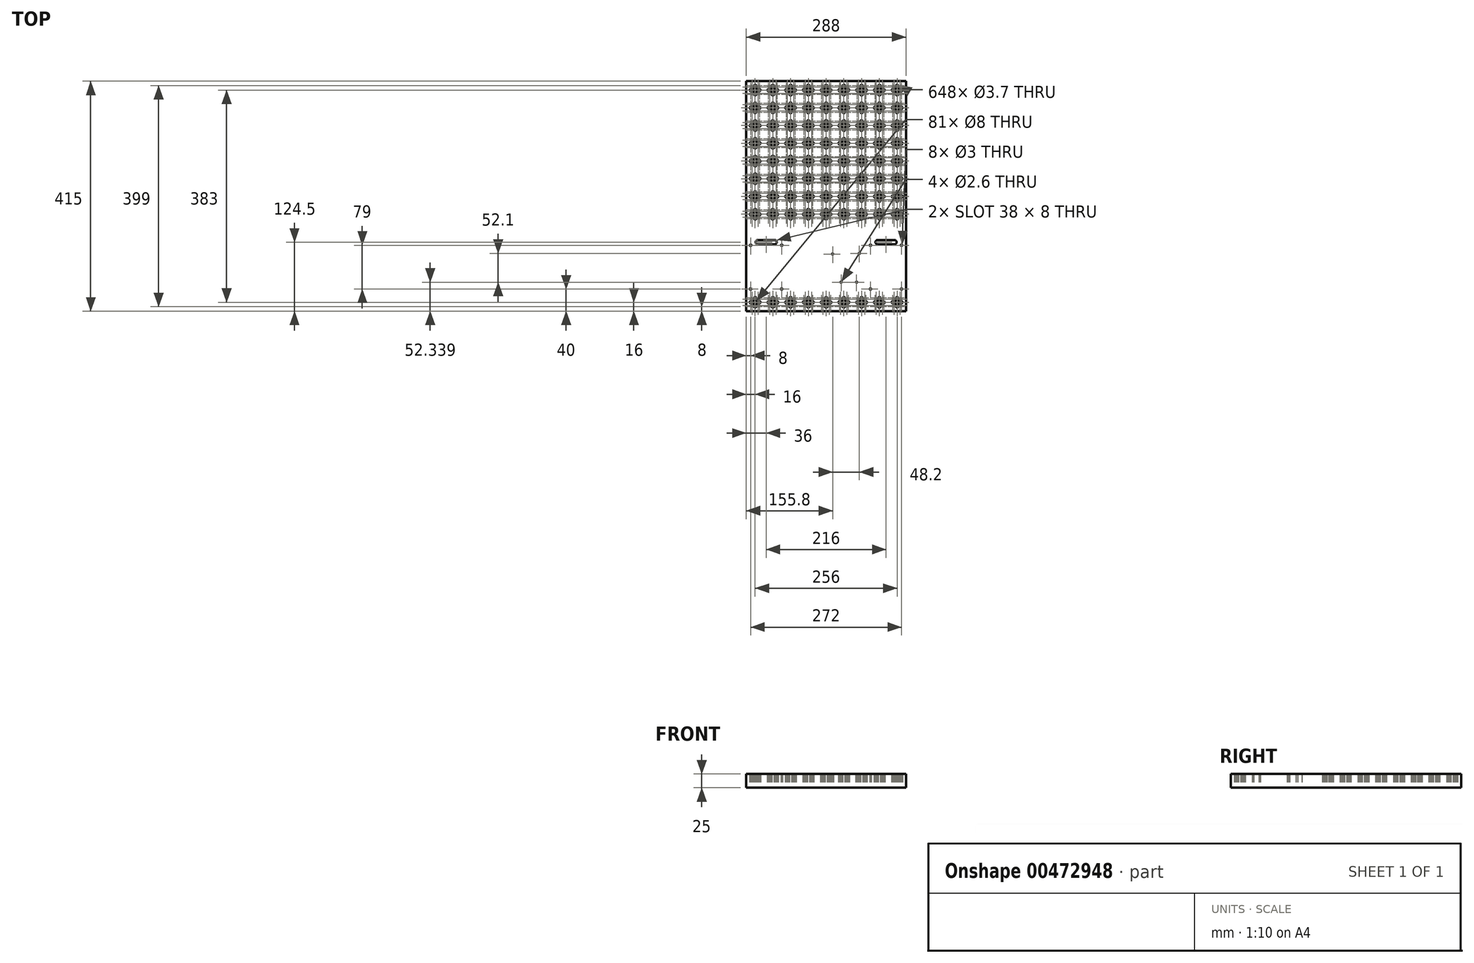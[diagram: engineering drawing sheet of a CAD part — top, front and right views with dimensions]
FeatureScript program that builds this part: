
annotation { "Feature Type Name" : "Feature", "Feature Type Description" : "" }
export const myFeature = defineFeature(function(context is Context, id is Id, definition is map)
    precondition{}
    {
        {
            var Q0;
            Q0=qCreatedBy(makeId("Top.planeOp"),FACE);
            var sketch = newSketch(context, id + "F0", { "sketchPlane" : qUnion([Q0])});
            skLineSegment(sketch, "E0.bottom", {"start": v(0, 0) * mm, "end": v(288, 0) * mm});
            skLineSegment(sketch, "E0.top", {"start": v(0, -415) * mm, "end": v(288, -415) * mm});
            skLineSegment(sketch, "E0.left", {"start": v(0, 0) * mm, "end": v(0, -415) * mm});
            skLineSegment(sketch, "E0.right", {"start": v(288, 0) * mm, "end": v(288, -415) * mm});
            skCircle(sketch, "E1", {"center": v(16, -407) * mm, "radius": 1.85 * mm});
            skCircle(sketch, "E2", {"center": v(16, -399) * mm, "radius": 4 * mm});
            skCircle(sketch, "E3.1.0", {"center": v(21.66, -404.66) * mm, "radius": 1.85 * mm});
            skCircle(sketch, "E3.2.0", {"center": v(24, -399) * mm, "radius": 1.85 * mm});
            skCircle(sketch, "E3.3.0", {"center": v(21.66, -393.34) * mm, "radius": 1.85 * mm});
            skCircle(sketch, "E3.4.0", {"center": v(16, -391) * mm, "radius": 1.85 * mm});
            skCircle(sketch, "E3.5.0", {"center": v(10.34, -393.34) * mm, "radius": 1.85 * mm});
            skCircle(sketch, "E3.6.0", {"center": v(8, -399) * mm, "radius": 1.85 * mm});
            skCircle(sketch, "E3.7.0", {"center": v(10.34, -404.66) * mm, "radius": 1.85 * mm});
            skCircle(sketch, "E4.1.0.0", {"center": v(42.34, -404.66) * mm, "radius": 1.85 * mm});
            skPoint(sketch, "E4.1.0.1", {"position": v(48, -399) * mm});
            skCircle(sketch, "E4.1.0.2", {"center": v(48, -391) * mm, "radius": 1.85 * mm});
            skCircle(sketch, "E4.1.0.3", {"center": v(53.66, -393.34) * mm, "radius": 1.85 * mm});
            skCircle(sketch, "E4.1.0.4", {"center": v(56, -399) * mm, "radius": 1.85 * mm});
            skCircle(sketch, "E4.1.0.5", {"center": v(53.66, -404.66) * mm, "radius": 1.85 * mm});
            skCircle(sketch, "E4.1.0.6", {"center": v(48, -399) * mm, "radius": 4 * mm});
            skCircle(sketch, "E4.1.0.7", {"center": v(48, -407) * mm, "radius": 1.85 * mm});
            skCircle(sketch, "E4.1.0.8", {"center": v(42.34, -393.34) * mm, "radius": 1.85 * mm});
            skCircle(sketch, "E4.1.0.9", {"center": v(40, -399) * mm, "radius": 1.85 * mm});
            skCircle(sketch, "E4.2.0.0", {"center": v(74.34, -404.66) * mm, "radius": 1.85 * mm});
            skPoint(sketch, "E4.2.0.1", {"position": v(80, -399) * mm});
            skCircle(sketch, "E4.2.0.2", {"center": v(80, -391) * mm, "radius": 1.85 * mm});
            skCircle(sketch, "E4.2.0.3", {"center": v(85.66, -393.34) * mm, "radius": 1.85 * mm});
            skCircle(sketch, "E4.2.0.4", {"center": v(88, -399) * mm, "radius": 1.85 * mm});
            skCircle(sketch, "E4.2.0.5", {"center": v(85.66, -404.66) * mm, "radius": 1.85 * mm});
            skCircle(sketch, "E4.2.0.6", {"center": v(80, -399) * mm, "radius": 4 * mm});
            skCircle(sketch, "E4.2.0.7", {"center": v(80, -407) * mm, "radius": 1.85 * mm});
            skCircle(sketch, "E4.2.0.8", {"center": v(74.34, -393.34) * mm, "radius": 1.85 * mm});
            skCircle(sketch, "E4.2.0.9", {"center": v(72, -399) * mm, "radius": 1.85 * mm});
            skCircle(sketch, "E4.3.0.0", {"center": v(106.34, -404.66) * mm, "radius": 1.85 * mm});
            skPoint(sketch, "E4.3.0.1", {"position": v(112, -399) * mm});
            skCircle(sketch, "E4.3.0.2", {"center": v(112, -391) * mm, "radius": 1.85 * mm});
            skCircle(sketch, "E4.3.0.3", {"center": v(117.66, -393.34) * mm, "radius": 1.85 * mm});
            skCircle(sketch, "E4.3.0.4", {"center": v(120, -399) * mm, "radius": 1.85 * mm});
            skCircle(sketch, "E4.3.0.5", {"center": v(117.66, -404.66) * mm, "radius": 1.85 * mm});
            skCircle(sketch, "E4.3.0.6", {"center": v(112, -399) * mm, "radius": 4 * mm});
            skCircle(sketch, "E4.3.0.7", {"center": v(112, -407) * mm, "radius": 1.85 * mm});
            skCircle(sketch, "E4.3.0.8", {"center": v(106.34, -393.34) * mm, "radius": 1.85 * mm});
            skCircle(sketch, "E4.3.0.9", {"center": v(104, -399) * mm, "radius": 1.85 * mm});
            skCircle(sketch, "E4.4.0.0", {"center": v(138.34, -404.66) * mm, "radius": 1.85 * mm});
            skPoint(sketch, "E4.4.0.1", {"position": v(144, -399) * mm});
            skCircle(sketch, "E4.4.0.2", {"center": v(144, -391) * mm, "radius": 1.85 * mm});
            skCircle(sketch, "E4.4.0.3", {"center": v(149.66, -393.34) * mm, "radius": 1.85 * mm});
            skCircle(sketch, "E4.4.0.4", {"center": v(152, -399) * mm, "radius": 1.85 * mm});
            skCircle(sketch, "E4.4.0.5", {"center": v(149.66, -404.66) * mm, "radius": 1.85 * mm});
            skCircle(sketch, "E4.4.0.6", {"center": v(144, -399) * mm, "radius": 4 * mm});
            skCircle(sketch, "E4.4.0.7", {"center": v(144, -407) * mm, "radius": 1.85 * mm});
            skCircle(sketch, "E4.4.0.8", {"center": v(138.34, -393.34) * mm, "radius": 1.85 * mm});
            skCircle(sketch, "E4.4.0.9", {"center": v(136, -399) * mm, "radius": 1.85 * mm});
            skCircle(sketch, "E4.5.0.0", {"center": v(170.34, -404.66) * mm, "radius": 1.85 * mm});
            skPoint(sketch, "E4.5.0.1", {"position": v(176, -399) * mm});
            skCircle(sketch, "E4.5.0.2", {"center": v(176, -391) * mm, "radius": 1.85 * mm});
            skCircle(sketch, "E4.5.0.3", {"center": v(181.66, -393.34) * mm, "radius": 1.85 * mm});
            skCircle(sketch, "E4.5.0.4", {"center": v(184, -399) * mm, "radius": 1.85 * mm});
            skCircle(sketch, "E4.5.0.5", {"center": v(181.66, -404.66) * mm, "radius": 1.85 * mm});
            skCircle(sketch, "E4.5.0.6", {"center": v(176, -399) * mm, "radius": 4 * mm});
            skCircle(sketch, "E4.5.0.7", {"center": v(176, -407) * mm, "radius": 1.85 * mm});
            skCircle(sketch, "E4.5.0.8", {"center": v(170.34, -393.34) * mm, "radius": 1.85 * mm});
            skCircle(sketch, "E4.5.0.9", {"center": v(168, -399) * mm, "radius": 1.85 * mm});
            skCircle(sketch, "E4.6.0.0", {"center": v(202.34, -404.66) * mm, "radius": 1.85 * mm});
            skPoint(sketch, "E4.6.0.1", {"position": v(208, -399) * mm});
            skCircle(sketch, "E4.6.0.2", {"center": v(208, -391) * mm, "radius": 1.85 * mm});
            skCircle(sketch, "E4.6.0.3", {"center": v(213.66, -393.34) * mm, "radius": 1.85 * mm});
            skCircle(sketch, "E4.6.0.4", {"center": v(216, -399) * mm, "radius": 1.85 * mm});
            skCircle(sketch, "E4.6.0.5", {"center": v(213.66, -404.66) * mm, "radius": 1.85 * mm});
            skCircle(sketch, "E4.6.0.6", {"center": v(208, -399) * mm, "radius": 4 * mm});
            skCircle(sketch, "E4.6.0.7", {"center": v(208, -407) * mm, "radius": 1.85 * mm});
            skCircle(sketch, "E4.6.0.8", {"center": v(202.34, -393.34) * mm, "radius": 1.85 * mm});
            skCircle(sketch, "E4.6.0.9", {"center": v(200, -399) * mm, "radius": 1.85 * mm});
            skCircle(sketch, "E4.7.0.0", {"center": v(234.34, -404.66) * mm, "radius": 1.85 * mm});
            skPoint(sketch, "E4.7.0.1", {"position": v(240, -399) * mm});
            skCircle(sketch, "E4.7.0.2", {"center": v(240, -391) * mm, "radius": 1.85 * mm});
            skCircle(sketch, "E4.7.0.3", {"center": v(245.66, -393.34) * mm, "radius": 1.85 * mm});
            skCircle(sketch, "E4.7.0.4", {"center": v(248, -399) * mm, "radius": 1.85 * mm});
            skCircle(sketch, "E4.7.0.5", {"center": v(245.66, -404.66) * mm, "radius": 1.85 * mm});
            skCircle(sketch, "E4.7.0.6", {"center": v(240, -399) * mm, "radius": 4 * mm});
            skCircle(sketch, "E4.7.0.7", {"center": v(240, -407) * mm, "radius": 1.85 * mm});
            skCircle(sketch, "E4.7.0.8", {"center": v(234.34, -393.34) * mm, "radius": 1.85 * mm});
            skCircle(sketch, "E4.7.0.9", {"center": v(232, -399) * mm, "radius": 1.85 * mm});
            skCircle(sketch, "E4.8.0.0", {"center": v(266.34, -404.66) * mm, "radius": 1.85 * mm});
            skPoint(sketch, "E4.8.0.1", {"position": v(272, -399) * mm});
            skCircle(sketch, "E4.8.0.2", {"center": v(272, -391) * mm, "radius": 1.85 * mm});
            skCircle(sketch, "E4.8.0.3", {"center": v(277.66, -393.34) * mm, "radius": 1.85 * mm});
            skCircle(sketch, "E4.8.0.4", {"center": v(280, -399) * mm, "radius": 1.85 * mm});
            skCircle(sketch, "E4.8.0.5", {"center": v(277.66, -404.66) * mm, "radius": 1.85 * mm});
            skCircle(sketch, "E4.8.0.6", {"center": v(272, -399) * mm, "radius": 4 * mm});
            skCircle(sketch, "E4.8.0.7", {"center": v(272, -407) * mm, "radius": 1.85 * mm});
            skCircle(sketch, "E4.8.0.8", {"center": v(266.34, -393.34) * mm, "radius": 1.85 * mm});
            skCircle(sketch, "E4.8.0.9", {"center": v(264, -399) * mm, "radius": 1.85 * mm});
            skLineSegment(sketch, "E4.direction1", {"start": v(10.34, -404.66) * mm, "end": v(42.34, -404.66) * mm, "construction": true});
            skLineSegment(sketch, "E5", {"start": v(0, -207.5) * mm, "end": v(288, -207.5) * mm, "construction": true});
            skCircle(sketch, "E6.MirrorC", {"center": v(8, -16) * mm, "radius": 1.85 * mm});
            skCircle(sketch, "E7.MirrorC", {"center": v(48, -8) * mm, "radius": 1.85 * mm});
            skCircle(sketch, "E8.MirrorC", {"center": v(240, -16) * mm, "radius": 4 * mm});
            skCircle(sketch, "E9.MirrorC", {"center": v(53.66, -10.34) * mm, "radius": 1.85 * mm});
            skCircle(sketch, "E10.MirrorC", {"center": v(208, -16) * mm, "radius": 4 * mm});
            skCircle(sketch, "E11.MirrorC", {"center": v(144, -16) * mm, "radius": 4 * mm});
            skCircle(sketch, "E12.MirrorC", {"center": v(56, -16) * mm, "radius": 1.85 * mm});
            skCircle(sketch, "E13.MirrorC", {"center": v(112, -16) * mm, "radius": 4 * mm});
            skCircle(sketch, "E14.MirrorC", {"center": v(16, -16) * mm, "radius": 4 * mm});
            skCircle(sketch, "E15.MirrorC", {"center": v(10.34, -10.34) * mm, "radius": 1.85 * mm});
            skCircle(sketch, "E16.MirrorC", {"center": v(176, -16) * mm, "radius": 4 * mm});
            skCircle(sketch, "E17.MirrorC", {"center": v(42.34, -10.34) * mm, "radius": 1.85 * mm});
            skCircle(sketch, "E18.MirrorC", {"center": v(42.34, -21.66) * mm, "radius": 1.85 * mm});
            skCircle(sketch, "E19.MirrorC", {"center": v(277.66, -10.34) * mm, "radius": 1.85 * mm});
            skCircle(sketch, "E20.MirrorC", {"center": v(40, -16) * mm, "radius": 1.85 * mm});
            skCircle(sketch, "E21.MirrorC", {"center": v(80, -16) * mm, "radius": 4 * mm});
            skCircle(sketch, "E22.MirrorC", {"center": v(272, -16) * mm, "radius": 4 * mm});
            skCircle(sketch, "E23.MirrorC", {"center": v(48, -16) * mm, "radius": 4 * mm});
            skCircle(sketch, "E24.MirrorC", {"center": v(272, -8) * mm, "radius": 1.85 * mm});
            skCircle(sketch, "E25.MirrorC", {"center": v(21.66, -21.66) * mm, "radius": 1.85 * mm});
            skCircle(sketch, "E26.MirrorC", {"center": v(10.34, -21.66) * mm, "radius": 1.85 * mm});
            skCircle(sketch, "E27.MirrorC", {"center": v(117.66, -21.66) * mm, "radius": 1.85 * mm});
            skCircle(sketch, "E28.MirrorC", {"center": v(74.34, -10.34) * mm, "radius": 1.85 * mm});
            skCircle(sketch, "E29.MirrorC", {"center": v(234.34, -21.66) * mm, "radius": 1.85 * mm});
            skCircle(sketch, "E30.MirrorC", {"center": v(248, -16) * mm, "radius": 1.85 * mm});
            skCircle(sketch, "E31.MirrorC", {"center": v(117.66, -10.34) * mm, "radius": 1.85 * mm});
            skCircle(sketch, "E32.MirrorC", {"center": v(280, -16) * mm, "radius": 1.85 * mm});
            skCircle(sketch, "E33.MirrorC", {"center": v(176, -8) * mm, "radius": 1.85 * mm});
            skCircle(sketch, "E34.MirrorC", {"center": v(176, -24) * mm, "radius": 1.85 * mm});
            skCircle(sketch, "E35.MirrorC", {"center": v(104, -16) * mm, "radius": 1.85 * mm});
            skLineSegment(sketch, "E36.MirrorCS", {"start": v(10.34, -10.34) * mm, "end": v(42.34, -10.34) * mm, "construction": true});
            skCircle(sketch, "E37.MirrorC", {"center": v(112, -8) * mm, "radius": 1.85 * mm});
            skCircle(sketch, "E38.MirrorC", {"center": v(181.66, -10.34) * mm, "radius": 1.85 * mm});
            skCircle(sketch, "E39.MirrorC", {"center": v(72, -16) * mm, "radius": 1.85 * mm});
            skCircle(sketch, "E40.MirrorC", {"center": v(85.66, -21.66) * mm, "radius": 1.85 * mm});
            skCircle(sketch, "E41.MirrorC", {"center": v(245.66, -10.34) * mm, "radius": 1.85 * mm});
            skCircle(sketch, "E42.MirrorC", {"center": v(264, -16) * mm, "radius": 1.85 * mm});
            skCircle(sketch, "E43.MirrorC", {"center": v(272, -24) * mm, "radius": 1.85 * mm});
            skCircle(sketch, "E44.MirrorC", {"center": v(74.34, -21.66) * mm, "radius": 1.85 * mm});
            skCircle(sketch, "E45.MirrorC", {"center": v(149.66, -10.34) * mm, "radius": 1.85 * mm});
            skCircle(sketch, "E46.MirrorC", {"center": v(120, -16) * mm, "radius": 1.85 * mm});
            skCircle(sketch, "E47.MirrorC", {"center": v(80, -8) * mm, "radius": 1.85 * mm});
            skCircle(sketch, "E48.MirrorC", {"center": v(24, -16) * mm, "radius": 1.85 * mm});
            skCircle(sketch, "E49.MirrorC", {"center": v(16, -24) * mm, "radius": 1.85 * mm});
            skCircle(sketch, "E50.MirrorC", {"center": v(112, -24) * mm, "radius": 1.85 * mm});
            skCircle(sketch, "E51.MirrorC", {"center": v(138.34, -21.66) * mm, "radius": 1.85 * mm});
            skCircle(sketch, "E52.MirrorC", {"center": v(106.34, -10.34) * mm, "radius": 1.85 * mm});
            skCircle(sketch, "E53.MirrorC", {"center": v(106.34, -21.66) * mm, "radius": 1.85 * mm});
            skCircle(sketch, "E54.MirrorC", {"center": v(232, -16) * mm, "radius": 1.85 * mm});
            skCircle(sketch, "E55.MirrorC", {"center": v(152, -16) * mm, "radius": 1.85 * mm});
            skCircle(sketch, "E56.MirrorC", {"center": v(168, -16) * mm, "radius": 1.85 * mm});
            skCircle(sketch, "E57.MirrorC", {"center": v(48, -24) * mm, "radius": 1.85 * mm});
            skCircle(sketch, "E58.MirrorC", {"center": v(202.34, -21.66) * mm, "radius": 1.85 * mm});
            skCircle(sketch, "E59.MirrorC", {"center": v(53.66, -21.66) * mm, "radius": 1.85 * mm});
            skCircle(sketch, "E60.MirrorC", {"center": v(202.34, -10.34) * mm, "radius": 1.85 * mm});
            skCircle(sketch, "E61.MirrorC", {"center": v(85.66, -10.34) * mm, "radius": 1.85 * mm});
            skCircle(sketch, "E62.MirrorC", {"center": v(149.66, -21.66) * mm, "radius": 1.85 * mm});
            skCircle(sketch, "E63.MirrorC", {"center": v(170.34, -10.34) * mm, "radius": 1.85 * mm});
            skCircle(sketch, "E64.MirrorC", {"center": v(234.34, -10.34) * mm, "radius": 1.85 * mm});
            skCircle(sketch, "E65.MirrorC", {"center": v(266.34, -21.66) * mm, "radius": 1.85 * mm});
            skCircle(sketch, "E66.MirrorC", {"center": v(181.66, -21.66) * mm, "radius": 1.85 * mm});
            skCircle(sketch, "E67.MirrorC", {"center": v(88, -16) * mm, "radius": 1.85 * mm});
            skCircle(sketch, "E68.MirrorC", {"center": v(213.66, -21.66) * mm, "radius": 1.85 * mm});
            skCircle(sketch, "E69.MirrorC", {"center": v(266.34, -10.34) * mm, "radius": 1.85 * mm});
            skCircle(sketch, "E70.MirrorC", {"center": v(208, -8) * mm, "radius": 1.85 * mm});
            skCircle(sketch, "E71.MirrorC", {"center": v(136, -16) * mm, "radius": 1.85 * mm});
            skCircle(sketch, "E72.MirrorC", {"center": v(208, -24) * mm, "radius": 1.85 * mm});
            skCircle(sketch, "E73.MirrorC", {"center": v(277.66, -21.66) * mm, "radius": 1.85 * mm});
            skCircle(sketch, "E74.MirrorC", {"center": v(240, -24) * mm, "radius": 1.85 * mm});
            skCircle(sketch, "E75.MirrorC", {"center": v(144, -8) * mm, "radius": 1.85 * mm});
            skCircle(sketch, "E76.MirrorC", {"center": v(138.34, -10.34) * mm, "radius": 1.85 * mm});
            skCircle(sketch, "E77.MirrorC", {"center": v(80, -24) * mm, "radius": 1.85 * mm});
            skCircle(sketch, "E78.MirrorC", {"center": v(21.66, -10.34) * mm, "radius": 1.85 * mm});
            skCircle(sketch, "E79.MirrorC", {"center": v(16, -8) * mm, "radius": 1.85 * mm});
            skCircle(sketch, "E80.MirrorC", {"center": v(170.34, -21.66) * mm, "radius": 1.85 * mm});
            skCircle(sketch, "E81.MirrorC", {"center": v(200, -16) * mm, "radius": 1.85 * mm});
            skCircle(sketch, "E82.MirrorC", {"center": v(245.66, -21.66) * mm, "radius": 1.85 * mm});
            skCircle(sketch, "E83.MirrorC", {"center": v(213.66, -10.34) * mm, "radius": 1.85 * mm});
            skCircle(sketch, "E84.MirrorC", {"center": v(240, -8) * mm, "radius": 1.85 * mm});
            skCircle(sketch, "E85.MirrorC", {"center": v(144, -24) * mm, "radius": 1.85 * mm});
            skCircle(sketch, "E86.MirrorC", {"center": v(216, -16) * mm, "radius": 1.85 * mm});
            skCircle(sketch, "E87.MirrorC", {"center": v(184, -16) * mm, "radius": 1.85 * mm});
            skCircle(sketch, "E88", {"center": v(280, -375) * mm, "radius": 1.5 * mm});
            skCircle(sketch, "E89", {"center": v(280, -296) * mm, "radius": 1.5 * mm});
            skCircle(sketch, "E90", {"center": v(224, -296) * mm, "radius": 1.5 * mm});
            skCircle(sketch, "E91", {"center": v(224, -375) * mm, "radius": 1.5 * mm});
            skPoint(sketch, "E92.startSnap0", {"position": v(144, 0) * mm});
            skLineSegment(sketch, "E93", {"start": v(144, 0) * mm, "end": v(144, -415) * mm, "construction": true});
            skCircle(sketch, "E94.MirrorC", {"center": v(8, -375) * mm, "radius": 1.5 * mm});
            skCircle(sketch, "E95.MirrorC", {"center": v(64, -296) * mm, "radius": 1.5 * mm});
            skCircle(sketch, "E96.MirrorC", {"center": v(64, -375) * mm, "radius": 1.5 * mm});
            skCircle(sketch, "E97.MirrorC", {"center": v(8, -296) * mm, "radius": 1.5 * mm});
            skLineSegment(sketch, "E98.bottom", {"start": v(267, -286.5) * mm, "end": v(237, -286.5) * mm});
            skLineSegment(sketch, "E98.top", {"start": v(267, -294.5) * mm, "end": v(237, -294.5) * mm});
            skLineSegment(sketch, "E98.left", {"start": v(271, -290.5) * mm, "end": v(271, -290.5) * mm});
            skLineSegment(sketch, "E98.right", {"start": v(233, -290.5) * mm, "end": v(233, -290.5) * mm});
            skLineSegment(sketch, "E99.MirrorCS", {"start": v(17, -290.5) * mm, "end": v(17, -290.5) * mm});
            skLineSegment(sketch, "E100.MirrorCS", {"start": v(55, -290.5) * mm, "end": v(55, -290.5) * mm});
            skLineSegment(sketch, "E101.MirrorCS", {"start": v(21, -286.5) * mm, "end": v(51, -286.5) * mm});
            skLineSegment(sketch, "E102.MirrorCS", {"start": v(21, -294.5) * mm, "end": v(51, -294.5) * mm});
            skPoint(sketch, "E103.visualSharp", {"position": v(233, -286.5) * mm});
            skArc(sketch, "E103.filletArc", {"start": v(237, -286.5) * mm, "mid": v(234.17, -287.67) * mm, "end": v(233, -290.5) * mm});
            skPoint(sketch, "E104.visualSharp", {"position": v(271, -294.5) * mm});
            skArc(sketch, "E104.filletArc", {"start": v(267, -294.5) * mm, "mid": v(269.83, -293.33) * mm, "end": v(271, -290.5) * mm});
            skPoint(sketch, "E105.visualSharp", {"position": v(233, -294.5) * mm});
            skArc(sketch, "E105.filletArc", {"start": v(233, -290.5) * mm, "mid": v(234.17, -293.33) * mm, "end": v(237, -294.5) * mm});
            skPoint(sketch, "E106.visualSharp", {"position": v(55, -286.5) * mm});
            skArc(sketch, "E106.filletArc", {"start": v(55, -290.5) * mm, "mid": v(53.83, -287.67) * mm, "end": v(51, -286.5) * mm});
            skPoint(sketch, "E107.visualSharp", {"position": v(17, -294.5) * mm});
            skArc(sketch, "E107.filletArc", {"start": v(17, -290.5) * mm, "mid": v(18.17, -293.33) * mm, "end": v(21, -294.5) * mm});
            skPoint(sketch, "E108.visualSharp", {"position": v(55, -294.5) * mm});
            skArc(sketch, "E108.filletArc", {"start": v(51, -294.5) * mm, "mid": v(53.83, -293.33) * mm, "end": v(55, -290.5) * mm});
            skPoint(sketch, "E109.visualSharp", {"position": v(17, -286.5) * mm});
            skArc(sketch, "E109.filletArc", {"start": v(21, -286.5) * mm, "mid": v(18.17, -287.67) * mm, "end": v(17, -290.5) * mm});
            skPoint(sketch, "E110.visualSharp", {"position": v(271, -286.5) * mm});
            skArc(sketch, "E110.filletArc", {"start": v(271, -290.5) * mm, "mid": v(269.83, -287.67) * mm, "end": v(267, -286.5) * mm});
            skSolve(sketch);
        }
        {
            var Q0;
            Q0=makeQuery(id+"F0.imprint","IMPRINT",FACE,{"disambiguationData":[TD([[makeQuery(id+"F0.imprint","IMPRINT",EDGE,{"derivedFrom":sQuery(id+"F0.wireOp",EDGE,"E0.bottom")}),-1.0]])]});
            var sketch = newSketch(context, id + "F1", { "sketchPlane" : qUnion([Q0])});
            skCircle(sketch, "E111", {"center": v(24, -48) * mm, "radius": 1.85 * mm});
            skCircle(sketch, "E112", {"center": v(16, -48) * mm, "radius": 4 * mm});
            skCircle(sketch, "E113.1.0", {"center": v(21.66, -42.34) * mm, "radius": 1.85 * mm});
            skCircle(sketch, "E113.2.0", {"center": v(16, -40) * mm, "radius": 1.85 * mm});
            skCircle(sketch, "E114.1.3.0", {"center": v(10.34, -42.34) * mm, "radius": 1.85 * mm});
            skCircle(sketch, "E114.1.4.0", {"center": v(8, -48) * mm, "radius": 1.85 * mm});
            skCircle(sketch, "E114.1.5.0", {"center": v(10.34, -53.66) * mm, "radius": 1.85 * mm});
            skCircle(sketch, "E114.1.6.0", {"center": v(16, -56) * mm, "radius": 1.85 * mm});
            skCircle(sketch, "E114.1.7.0", {"center": v(21.66, -53.66) * mm, "radius": 1.85 * mm});
            skCircle(sketch, "E115.0.1.0", {"center": v(16, -80) * mm, "radius": 4 * mm});
            skCircle(sketch, "E115.0.1.1", {"center": v(16, -72) * mm, "radius": 1.85 * mm});
            skCircle(sketch, "E115.0.1.2", {"center": v(21.66, -74.34) * mm, "radius": 1.85 * mm});
            skCircle(sketch, "E115.0.1.3", {"center": v(24, -80) * mm, "radius": 1.85 * mm});
            skCircle(sketch, "E115.0.1.4", {"center": v(21.66, -85.66) * mm, "radius": 1.85 * mm});
            skCircle(sketch, "E115.0.1.5", {"center": v(16, -88) * mm, "radius": 1.85 * mm});
            skCircle(sketch, "E115.0.1.6", {"center": v(10.34, -85.66) * mm, "radius": 1.85 * mm});
            skCircle(sketch, "E115.0.1.7", {"center": v(8, -80) * mm, "radius": 1.85 * mm});
            skCircle(sketch, "E115.0.1.8", {"center": v(10.34, -74.34) * mm, "radius": 1.85 * mm});
            skCircle(sketch, "E115.0.2.0", {"center": v(16, -112) * mm, "radius": 4 * mm});
            skCircle(sketch, "E115.0.2.1", {"center": v(16, -104) * mm, "radius": 1.85 * mm});
            skCircle(sketch, "E115.0.2.2", {"center": v(21.66, -106.34) * mm, "radius": 1.85 * mm});
            skCircle(sketch, "E115.0.2.3", {"center": v(24, -112) * mm, "radius": 1.85 * mm});
            skCircle(sketch, "E115.0.2.4", {"center": v(21.66, -117.66) * mm, "radius": 1.85 * mm});
            skCircle(sketch, "E115.0.2.5", {"center": v(16, -120) * mm, "radius": 1.85 * mm});
            skCircle(sketch, "E115.0.2.6", {"center": v(10.34, -117.66) * mm, "radius": 1.85 * mm});
            skCircle(sketch, "E115.0.2.7", {"center": v(8, -112) * mm, "radius": 1.85 * mm});
            skCircle(sketch, "E115.0.2.8", {"center": v(10.34, -106.34) * mm, "radius": 1.85 * mm});
            skCircle(sketch, "E115.0.3.0", {"center": v(16, -144) * mm, "radius": 4 * mm});
            skCircle(sketch, "E115.0.3.1", {"center": v(16, -136) * mm, "radius": 1.85 * mm});
            skCircle(sketch, "E115.0.3.2", {"center": v(21.66, -138.34) * mm, "radius": 1.85 * mm});
            skCircle(sketch, "E115.0.3.3", {"center": v(24, -144) * mm, "radius": 1.85 * mm});
            skCircle(sketch, "E115.0.3.4", {"center": v(21.66, -149.66) * mm, "radius": 1.85 * mm});
            skCircle(sketch, "E115.0.3.5", {"center": v(16, -152) * mm, "radius": 1.85 * mm});
            skCircle(sketch, "E115.0.3.6", {"center": v(10.34, -149.66) * mm, "radius": 1.85 * mm});
            skCircle(sketch, "E115.0.3.7", {"center": v(8, -144) * mm, "radius": 1.85 * mm});
            skCircle(sketch, "E115.0.3.8", {"center": v(10.34, -138.34) * mm, "radius": 1.85 * mm});
            skCircle(sketch, "E115.0.4.0", {"center": v(16, -176) * mm, "radius": 4 * mm});
            skCircle(sketch, "E115.0.4.1", {"center": v(16, -168) * mm, "radius": 1.85 * mm});
            skCircle(sketch, "E115.0.4.2", {"center": v(21.66, -170.34) * mm, "radius": 1.85 * mm});
            skCircle(sketch, "E115.0.4.3", {"center": v(24, -176) * mm, "radius": 1.85 * mm});
            skCircle(sketch, "E115.0.4.4", {"center": v(21.66, -181.66) * mm, "radius": 1.85 * mm});
            skCircle(sketch, "E115.0.4.5", {"center": v(16, -184) * mm, "radius": 1.85 * mm});
            skCircle(sketch, "E115.0.4.6", {"center": v(10.34, -181.66) * mm, "radius": 1.85 * mm});
            skCircle(sketch, "E115.0.4.7", {"center": v(8, -176) * mm, "radius": 1.85 * mm});
            skCircle(sketch, "E115.0.4.8", {"center": v(10.34, -170.34) * mm, "radius": 1.85 * mm});
            skCircle(sketch, "E115.0.5.0", {"center": v(16, -208) * mm, "radius": 4 * mm});
            skCircle(sketch, "E115.0.5.1", {"center": v(16, -200) * mm, "radius": 1.85 * mm});
            skCircle(sketch, "E115.0.5.2", {"center": v(21.66, -202.34) * mm, "radius": 1.85 * mm});
            skCircle(sketch, "E115.0.5.3", {"center": v(24, -208) * mm, "radius": 1.85 * mm});
            skCircle(sketch, "E115.0.5.4", {"center": v(21.66, -213.66) * mm, "radius": 1.85 * mm});
            skCircle(sketch, "E115.0.5.5", {"center": v(16, -216) * mm, "radius": 1.85 * mm});
            skCircle(sketch, "E115.0.5.6", {"center": v(10.34, -213.66) * mm, "radius": 1.85 * mm});
            skCircle(sketch, "E115.0.5.7", {"center": v(8, -208) * mm, "radius": 1.85 * mm});
            skCircle(sketch, "E115.0.5.8", {"center": v(10.34, -202.34) * mm, "radius": 1.85 * mm});
            skCircle(sketch, "E115.0.6.0", {"center": v(16, -240) * mm, "radius": 4 * mm});
            skCircle(sketch, "E115.0.6.1", {"center": v(16, -232) * mm, "radius": 1.85 * mm});
            skCircle(sketch, "E115.0.6.2", {"center": v(21.66, -234.34) * mm, "radius": 1.85 * mm});
            skCircle(sketch, "E115.0.6.3", {"center": v(24, -240) * mm, "radius": 1.85 * mm});
            skCircle(sketch, "E115.0.6.4", {"center": v(21.66, -245.66) * mm, "radius": 1.85 * mm});
            skCircle(sketch, "E115.0.6.5", {"center": v(16, -248) * mm, "radius": 1.85 * mm});
            skCircle(sketch, "E115.0.6.6", {"center": v(10.34, -245.66) * mm, "radius": 1.85 * mm});
            skCircle(sketch, "E115.0.6.7", {"center": v(8, -240) * mm, "radius": 1.85 * mm});
            skCircle(sketch, "E115.0.6.8", {"center": v(10.34, -234.34) * mm, "radius": 1.85 * mm});
            skCircle(sketch, "E115.1.0.0", {"center": v(48, -48) * mm, "radius": 4 * mm});
            skCircle(sketch, "E115.1.0.1", {"center": v(48, -40) * mm, "radius": 1.85 * mm});
            skCircle(sketch, "E115.1.0.2", {"center": v(53.66, -42.34) * mm, "radius": 1.85 * mm});
            skCircle(sketch, "E115.1.0.3", {"center": v(56, -48) * mm, "radius": 1.85 * mm});
            skCircle(sketch, "E115.1.0.4", {"center": v(53.66, -53.66) * mm, "radius": 1.85 * mm});
            skCircle(sketch, "E115.1.0.5", {"center": v(48, -56) * mm, "radius": 1.85 * mm});
            skCircle(sketch, "E115.1.0.6", {"center": v(42.34, -53.66) * mm, "radius": 1.85 * mm});
            skCircle(sketch, "E115.1.0.7", {"center": v(40, -48) * mm, "radius": 1.85 * mm});
            skCircle(sketch, "E115.1.0.8", {"center": v(42.34, -42.34) * mm, "radius": 1.85 * mm});
            skCircle(sketch, "E115.1.1.0", {"center": v(48, -80) * mm, "radius": 4 * mm});
            skCircle(sketch, "E115.1.1.1", {"center": v(48, -72) * mm, "radius": 1.85 * mm});
            skCircle(sketch, "E115.1.1.2", {"center": v(53.66, -74.34) * mm, "radius": 1.85 * mm});
            skCircle(sketch, "E115.1.1.3", {"center": v(56, -80) * mm, "radius": 1.85 * mm});
            skCircle(sketch, "E115.1.1.4", {"center": v(53.66, -85.66) * mm, "radius": 1.85 * mm});
            skCircle(sketch, "E115.1.1.5", {"center": v(48, -88) * mm, "radius": 1.85 * mm});
            skCircle(sketch, "E115.1.1.6", {"center": v(42.34, -85.66) * mm, "radius": 1.85 * mm});
            skCircle(sketch, "E115.1.1.7", {"center": v(40, -80) * mm, "radius": 1.85 * mm});
            skCircle(sketch, "E115.1.1.8", {"center": v(42.34, -74.34) * mm, "radius": 1.85 * mm});
            skCircle(sketch, "E115.1.2.0", {"center": v(48, -112) * mm, "radius": 4 * mm});
            skCircle(sketch, "E115.1.2.1", {"center": v(48, -104) * mm, "radius": 1.85 * mm});
            skCircle(sketch, "E115.1.2.2", {"center": v(53.66, -106.34) * mm, "radius": 1.85 * mm});
            skCircle(sketch, "E115.1.2.3", {"center": v(56, -112) * mm, "radius": 1.85 * mm});
            skCircle(sketch, "E115.1.2.4", {"center": v(53.66, -117.66) * mm, "radius": 1.85 * mm});
            skCircle(sketch, "E115.1.2.5", {"center": v(48, -120) * mm, "radius": 1.85 * mm});
            skCircle(sketch, "E115.1.2.6", {"center": v(42.34, -117.66) * mm, "radius": 1.85 * mm});
            skCircle(sketch, "E115.1.2.7", {"center": v(40, -112) * mm, "radius": 1.85 * mm});
            skCircle(sketch, "E115.1.2.8", {"center": v(42.34, -106.34) * mm, "radius": 1.85 * mm});
            skCircle(sketch, "E115.1.3.0", {"center": v(48, -144) * mm, "radius": 4 * mm});
            skCircle(sketch, "E115.1.3.1", {"center": v(48, -136) * mm, "radius": 1.85 * mm});
            skCircle(sketch, "E115.1.3.2", {"center": v(53.66, -138.34) * mm, "radius": 1.85 * mm});
            skCircle(sketch, "E115.1.3.3", {"center": v(56, -144) * mm, "radius": 1.85 * mm});
            skCircle(sketch, "E115.1.3.4", {"center": v(53.66, -149.66) * mm, "radius": 1.85 * mm});
            skCircle(sketch, "E115.1.3.5", {"center": v(48, -152) * mm, "radius": 1.85 * mm});
            skCircle(sketch, "E115.1.3.6", {"center": v(42.34, -149.66) * mm, "radius": 1.85 * mm});
            skCircle(sketch, "E115.1.3.7", {"center": v(40, -144) * mm, "radius": 1.85 * mm});
            skCircle(sketch, "E115.1.3.8", {"center": v(42.34, -138.34) * mm, "radius": 1.85 * mm});
            skCircle(sketch, "E115.1.4.0", {"center": v(48, -176) * mm, "radius": 4 * mm});
            skCircle(sketch, "E115.1.4.1", {"center": v(48, -168) * mm, "radius": 1.85 * mm});
            skCircle(sketch, "E115.1.4.2", {"center": v(53.66, -170.34) * mm, "radius": 1.85 * mm});
            skCircle(sketch, "E115.1.4.3", {"center": v(56, -176) * mm, "radius": 1.85 * mm});
            skCircle(sketch, "E115.1.4.4", {"center": v(53.66, -181.66) * mm, "radius": 1.85 * mm});
            skCircle(sketch, "E115.1.4.5", {"center": v(48, -184) * mm, "radius": 1.85 * mm});
            skCircle(sketch, "E115.1.4.6", {"center": v(42.34, -181.66) * mm, "radius": 1.85 * mm});
            skCircle(sketch, "E115.1.4.7", {"center": v(40, -176) * mm, "radius": 1.85 * mm});
            skCircle(sketch, "E115.1.4.8", {"center": v(42.34, -170.34) * mm, "radius": 1.85 * mm});
            skCircle(sketch, "E115.1.5.0", {"center": v(48, -208) * mm, "radius": 4 * mm});
            skCircle(sketch, "E115.1.5.1", {"center": v(48, -200) * mm, "radius": 1.85 * mm});
            skCircle(sketch, "E115.1.5.2", {"center": v(53.66, -202.34) * mm, "radius": 1.85 * mm});
            skCircle(sketch, "E115.1.5.3", {"center": v(56, -208) * mm, "radius": 1.85 * mm});
            skCircle(sketch, "E115.1.5.4", {"center": v(53.66, -213.66) * mm, "radius": 1.85 * mm});
            skCircle(sketch, "E115.1.5.5", {"center": v(48, -216) * mm, "radius": 1.85 * mm});
            skCircle(sketch, "E115.1.5.6", {"center": v(42.34, -213.66) * mm, "radius": 1.85 * mm});
            skCircle(sketch, "E115.1.5.7", {"center": v(40, -208) * mm, "radius": 1.85 * mm});
            skCircle(sketch, "E115.1.5.8", {"center": v(42.34, -202.34) * mm, "radius": 1.85 * mm});
            skCircle(sketch, "E115.1.6.0", {"center": v(48, -240) * mm, "radius": 4 * mm});
            skCircle(sketch, "E115.1.6.1", {"center": v(48, -232) * mm, "radius": 1.85 * mm});
            skCircle(sketch, "E115.1.6.2", {"center": v(53.66, -234.34) * mm, "radius": 1.85 * mm});
            skCircle(sketch, "E115.1.6.3", {"center": v(56, -240) * mm, "radius": 1.85 * mm});
            skCircle(sketch, "E115.1.6.4", {"center": v(53.66, -245.66) * mm, "radius": 1.85 * mm});
            skCircle(sketch, "E115.1.6.5", {"center": v(48, -248) * mm, "radius": 1.85 * mm});
            skCircle(sketch, "E115.1.6.6", {"center": v(42.34, -245.66) * mm, "radius": 1.85 * mm});
            skCircle(sketch, "E115.1.6.7", {"center": v(40, -240) * mm, "radius": 1.85 * mm});
            skCircle(sketch, "E115.1.6.8", {"center": v(42.34, -234.34) * mm, "radius": 1.85 * mm});
            skCircle(sketch, "E115.2.0.0", {"center": v(80, -48) * mm, "radius": 4 * mm});
            skCircle(sketch, "E115.2.0.1", {"center": v(80, -40) * mm, "radius": 1.85 * mm});
            skCircle(sketch, "E115.2.0.2", {"center": v(85.66, -42.34) * mm, "radius": 1.85 * mm});
            skCircle(sketch, "E115.2.0.3", {"center": v(88, -48) * mm, "radius": 1.85 * mm});
            skCircle(sketch, "E115.2.0.4", {"center": v(85.66, -53.66) * mm, "radius": 1.85 * mm});
            skCircle(sketch, "E115.2.0.5", {"center": v(80, -56) * mm, "radius": 1.85 * mm});
            skCircle(sketch, "E115.2.0.6", {"center": v(74.34, -53.66) * mm, "radius": 1.85 * mm});
            skCircle(sketch, "E115.2.0.7", {"center": v(72, -48) * mm, "radius": 1.85 * mm});
            skCircle(sketch, "E115.2.0.8", {"center": v(74.34, -42.34) * mm, "radius": 1.85 * mm});
            skCircle(sketch, "E115.2.1.0", {"center": v(80, -80) * mm, "radius": 4 * mm});
            skCircle(sketch, "E115.2.1.1", {"center": v(80, -72) * mm, "radius": 1.85 * mm});
            skCircle(sketch, "E115.2.1.2", {"center": v(85.66, -74.34) * mm, "radius": 1.85 * mm});
            skCircle(sketch, "E115.2.1.3", {"center": v(88, -80) * mm, "radius": 1.85 * mm});
            skCircle(sketch, "E115.2.1.4", {"center": v(85.66, -85.66) * mm, "radius": 1.85 * mm});
            skCircle(sketch, "E115.2.1.5", {"center": v(80, -88) * mm, "radius": 1.85 * mm});
            skCircle(sketch, "E115.2.1.6", {"center": v(74.34, -85.66) * mm, "radius": 1.85 * mm});
            skCircle(sketch, "E115.2.1.7", {"center": v(72, -80) * mm, "radius": 1.85 * mm});
            skCircle(sketch, "E115.2.1.8", {"center": v(74.34, -74.34) * mm, "radius": 1.85 * mm});
            skCircle(sketch, "E115.2.2.0", {"center": v(80, -112) * mm, "radius": 4 * mm});
            skCircle(sketch, "E115.2.2.1", {"center": v(80, -104) * mm, "radius": 1.85 * mm});
            skCircle(sketch, "E115.2.2.2", {"center": v(85.66, -106.34) * mm, "radius": 1.85 * mm});
            skCircle(sketch, "E115.2.2.3", {"center": v(88, -112) * mm, "radius": 1.85 * mm});
            skCircle(sketch, "E115.2.2.4", {"center": v(85.66, -117.66) * mm, "radius": 1.85 * mm});
            skCircle(sketch, "E115.2.2.5", {"center": v(80, -120) * mm, "radius": 1.85 * mm});
            skCircle(sketch, "E115.2.2.6", {"center": v(74.34, -117.66) * mm, "radius": 1.85 * mm});
            skCircle(sketch, "E115.2.2.7", {"center": v(72, -112) * mm, "radius": 1.85 * mm});
            skCircle(sketch, "E115.2.2.8", {"center": v(74.34, -106.34) * mm, "radius": 1.85 * mm});
            skCircle(sketch, "E115.2.3.0", {"center": v(80, -144) * mm, "radius": 4 * mm});
            skCircle(sketch, "E115.2.3.1", {"center": v(80, -136) * mm, "radius": 1.85 * mm});
            skCircle(sketch, "E115.2.3.2", {"center": v(85.66, -138.34) * mm, "radius": 1.85 * mm});
            skCircle(sketch, "E115.2.3.3", {"center": v(88, -144) * mm, "radius": 1.85 * mm});
            skCircle(sketch, "E115.2.3.4", {"center": v(85.66, -149.66) * mm, "radius": 1.85 * mm});
            skCircle(sketch, "E115.2.3.5", {"center": v(80, -152) * mm, "radius": 1.85 * mm});
            skCircle(sketch, "E115.2.3.6", {"center": v(74.34, -149.66) * mm, "radius": 1.85 * mm});
            skCircle(sketch, "E115.2.3.7", {"center": v(72, -144) * mm, "radius": 1.85 * mm});
            skCircle(sketch, "E115.2.3.8", {"center": v(74.34, -138.34) * mm, "radius": 1.85 * mm});
            skCircle(sketch, "E115.2.4.0", {"center": v(80, -176) * mm, "radius": 4 * mm});
            skCircle(sketch, "E115.2.4.1", {"center": v(80, -168) * mm, "radius": 1.85 * mm});
            skCircle(sketch, "E115.2.4.2", {"center": v(85.66, -170.34) * mm, "radius": 1.85 * mm});
            skCircle(sketch, "E115.2.4.3", {"center": v(88, -176) * mm, "radius": 1.85 * mm});
            skCircle(sketch, "E115.2.4.4", {"center": v(85.66, -181.66) * mm, "radius": 1.85 * mm});
            skCircle(sketch, "E115.2.4.5", {"center": v(80, -184) * mm, "radius": 1.85 * mm});
            skCircle(sketch, "E115.2.4.6", {"center": v(74.34, -181.66) * mm, "radius": 1.85 * mm});
            skCircle(sketch, "E115.2.4.7", {"center": v(72, -176) * mm, "radius": 1.85 * mm});
            skCircle(sketch, "E115.2.4.8", {"center": v(74.34, -170.34) * mm, "radius": 1.85 * mm});
            skCircle(sketch, "E115.2.5.0", {"center": v(80, -208) * mm, "radius": 4 * mm});
            skCircle(sketch, "E115.2.5.1", {"center": v(80, -200) * mm, "radius": 1.85 * mm});
            skCircle(sketch, "E115.2.5.2", {"center": v(85.66, -202.34) * mm, "radius": 1.85 * mm});
            skCircle(sketch, "E115.2.5.3", {"center": v(88, -208) * mm, "radius": 1.85 * mm});
            skCircle(sketch, "E115.2.5.4", {"center": v(85.66, -213.66) * mm, "radius": 1.85 * mm});
            skCircle(sketch, "E115.2.5.5", {"center": v(80, -216) * mm, "radius": 1.85 * mm});
            skCircle(sketch, "E115.2.5.6", {"center": v(74.34, -213.66) * mm, "radius": 1.85 * mm});
            skCircle(sketch, "E115.2.5.7", {"center": v(72, -208) * mm, "radius": 1.85 * mm});
            skCircle(sketch, "E115.2.5.8", {"center": v(74.34, -202.34) * mm, "radius": 1.85 * mm});
            skCircle(sketch, "E115.2.6.0", {"center": v(80, -240) * mm, "radius": 4 * mm});
            skCircle(sketch, "E115.2.6.1", {"center": v(80, -232) * mm, "radius": 1.85 * mm});
            skCircle(sketch, "E115.2.6.2", {"center": v(85.66, -234.34) * mm, "radius": 1.85 * mm});
            skCircle(sketch, "E115.2.6.3", {"center": v(88, -240) * mm, "radius": 1.85 * mm});
            skCircle(sketch, "E115.2.6.4", {"center": v(85.66, -245.66) * mm, "radius": 1.85 * mm});
            skCircle(sketch, "E115.2.6.5", {"center": v(80, -248) * mm, "radius": 1.85 * mm});
            skCircle(sketch, "E115.2.6.6", {"center": v(74.34, -245.66) * mm, "radius": 1.85 * mm});
            skCircle(sketch, "E115.2.6.7", {"center": v(72, -240) * mm, "radius": 1.85 * mm});
            skCircle(sketch, "E115.2.6.8", {"center": v(74.34, -234.34) * mm, "radius": 1.85 * mm});
            skCircle(sketch, "E115.3.0.0", {"center": v(112, -48) * mm, "radius": 4 * mm});
            skCircle(sketch, "E115.3.0.1", {"center": v(112, -40) * mm, "radius": 1.85 * mm});
            skCircle(sketch, "E115.3.0.2", {"center": v(117.66, -42.34) * mm, "radius": 1.85 * mm});
            skCircle(sketch, "E115.3.0.3", {"center": v(120, -48) * mm, "radius": 1.85 * mm});
            skCircle(sketch, "E115.3.0.4", {"center": v(117.66, -53.66) * mm, "radius": 1.85 * mm});
            skCircle(sketch, "E115.3.0.5", {"center": v(112, -56) * mm, "radius": 1.85 * mm});
            skCircle(sketch, "E115.3.0.6", {"center": v(106.34, -53.66) * mm, "radius": 1.85 * mm});
            skCircle(sketch, "E115.3.0.7", {"center": v(104, -48) * mm, "radius": 1.85 * mm});
            skCircle(sketch, "E115.3.0.8", {"center": v(106.34, -42.34) * mm, "radius": 1.85 * mm});
            skCircle(sketch, "E115.3.1.0", {"center": v(112, -80) * mm, "radius": 4 * mm});
            skCircle(sketch, "E115.3.1.1", {"center": v(112, -72) * mm, "radius": 1.85 * mm});
            skCircle(sketch, "E115.3.1.2", {"center": v(117.66, -74.34) * mm, "radius": 1.85 * mm});
            skCircle(sketch, "E115.3.1.3", {"center": v(120, -80) * mm, "radius": 1.85 * mm});
            skCircle(sketch, "E115.3.1.4", {"center": v(117.66, -85.66) * mm, "radius": 1.85 * mm});
            skCircle(sketch, "E115.3.1.5", {"center": v(112, -88) * mm, "radius": 1.85 * mm});
            skCircle(sketch, "E115.3.1.6", {"center": v(106.34, -85.66) * mm, "radius": 1.85 * mm});
            skCircle(sketch, "E115.3.1.7", {"center": v(104, -80) * mm, "radius": 1.85 * mm});
            skCircle(sketch, "E115.3.1.8", {"center": v(106.34, -74.34) * mm, "radius": 1.85 * mm});
            skCircle(sketch, "E115.3.2.0", {"center": v(112, -112) * mm, "radius": 4 * mm});
            skCircle(sketch, "E115.3.2.1", {"center": v(112, -104) * mm, "radius": 1.85 * mm});
            skCircle(sketch, "E115.3.2.2", {"center": v(117.66, -106.34) * mm, "radius": 1.85 * mm});
            skCircle(sketch, "E115.3.2.3", {"center": v(120, -112) * mm, "radius": 1.85 * mm});
            skCircle(sketch, "E115.3.2.4", {"center": v(117.66, -117.66) * mm, "radius": 1.85 * mm});
            skCircle(sketch, "E115.3.2.5", {"center": v(112, -120) * mm, "radius": 1.85 * mm});
            skCircle(sketch, "E115.3.2.6", {"center": v(106.34, -117.66) * mm, "radius": 1.85 * mm});
            skCircle(sketch, "E115.3.2.7", {"center": v(104, -112) * mm, "radius": 1.85 * mm});
            skCircle(sketch, "E115.3.2.8", {"center": v(106.34, -106.34) * mm, "radius": 1.85 * mm});
            skCircle(sketch, "E115.3.3.0", {"center": v(112, -144) * mm, "radius": 4 * mm});
            skCircle(sketch, "E115.3.3.1", {"center": v(112, -136) * mm, "radius": 1.85 * mm});
            skCircle(sketch, "E115.3.3.2", {"center": v(117.66, -138.34) * mm, "radius": 1.85 * mm});
            skCircle(sketch, "E115.3.3.3", {"center": v(120, -144) * mm, "radius": 1.85 * mm});
            skCircle(sketch, "E115.3.3.4", {"center": v(117.66, -149.66) * mm, "radius": 1.85 * mm});
            skCircle(sketch, "E115.3.3.5", {"center": v(112, -152) * mm, "radius": 1.85 * mm});
            skCircle(sketch, "E115.3.3.6", {"center": v(106.34, -149.66) * mm, "radius": 1.85 * mm});
            skCircle(sketch, "E115.3.3.7", {"center": v(104, -144) * mm, "radius": 1.85 * mm});
            skCircle(sketch, "E115.3.3.8", {"center": v(106.34, -138.34) * mm, "radius": 1.85 * mm});
            skCircle(sketch, "E115.3.4.0", {"center": v(112, -176) * mm, "radius": 4 * mm});
            skCircle(sketch, "E115.3.4.1", {"center": v(112, -168) * mm, "radius": 1.85 * mm});
            skCircle(sketch, "E115.3.4.2", {"center": v(117.66, -170.34) * mm, "radius": 1.85 * mm});
            skCircle(sketch, "E115.3.4.3", {"center": v(120, -176) * mm, "radius": 1.85 * mm});
            skCircle(sketch, "E115.3.4.4", {"center": v(117.66, -181.66) * mm, "radius": 1.85 * mm});
            skCircle(sketch, "E115.3.4.5", {"center": v(112, -184) * mm, "radius": 1.85 * mm});
            skCircle(sketch, "E115.3.4.6", {"center": v(106.34, -181.66) * mm, "radius": 1.85 * mm});
            skCircle(sketch, "E115.3.4.7", {"center": v(104, -176) * mm, "radius": 1.85 * mm});
            skCircle(sketch, "E115.3.4.8", {"center": v(106.34, -170.34) * mm, "radius": 1.85 * mm});
            skCircle(sketch, "E115.3.5.0", {"center": v(112, -208) * mm, "radius": 4 * mm});
            skCircle(sketch, "E115.3.5.1", {"center": v(112, -200) * mm, "radius": 1.85 * mm});
            skCircle(sketch, "E115.3.5.2", {"center": v(117.66, -202.34) * mm, "radius": 1.85 * mm});
            skCircle(sketch, "E115.3.5.3", {"center": v(120, -208) * mm, "radius": 1.85 * mm});
            skCircle(sketch, "E115.3.5.4", {"center": v(117.66, -213.66) * mm, "radius": 1.85 * mm});
            skCircle(sketch, "E115.3.5.5", {"center": v(112, -216) * mm, "radius": 1.85 * mm});
            skCircle(sketch, "E115.3.5.6", {"center": v(106.34, -213.66) * mm, "radius": 1.85 * mm});
            skCircle(sketch, "E115.3.5.7", {"center": v(104, -208) * mm, "radius": 1.85 * mm});
            skCircle(sketch, "E115.3.5.8", {"center": v(106.34, -202.34) * mm, "radius": 1.85 * mm});
            skCircle(sketch, "E115.3.6.0", {"center": v(112, -240) * mm, "radius": 4 * mm});
            skCircle(sketch, "E115.3.6.1", {"center": v(112, -232) * mm, "radius": 1.85 * mm});
            skCircle(sketch, "E115.3.6.2", {"center": v(117.66, -234.34) * mm, "radius": 1.85 * mm});
            skCircle(sketch, "E115.3.6.3", {"center": v(120, -240) * mm, "radius": 1.85 * mm});
            skCircle(sketch, "E115.3.6.4", {"center": v(117.66, -245.66) * mm, "radius": 1.85 * mm});
            skCircle(sketch, "E115.3.6.5", {"center": v(112, -248) * mm, "radius": 1.85 * mm});
            skCircle(sketch, "E115.3.6.6", {"center": v(106.34, -245.66) * mm, "radius": 1.85 * mm});
            skCircle(sketch, "E115.3.6.7", {"center": v(104, -240) * mm, "radius": 1.85 * mm});
            skCircle(sketch, "E115.3.6.8", {"center": v(106.34, -234.34) * mm, "radius": 1.85 * mm});
            skCircle(sketch, "E115.4.0.0", {"center": v(144, -48) * mm, "radius": 4 * mm});
            skCircle(sketch, "E115.4.0.1", {"center": v(144, -40) * mm, "radius": 1.85 * mm});
            skCircle(sketch, "E115.4.0.2", {"center": v(149.66, -42.34) * mm, "radius": 1.85 * mm});
            skCircle(sketch, "E115.4.0.3", {"center": v(152, -48) * mm, "radius": 1.85 * mm});
            skCircle(sketch, "E115.4.0.4", {"center": v(149.66, -53.66) * mm, "radius": 1.85 * mm});
            skCircle(sketch, "E115.4.0.5", {"center": v(144, -56) * mm, "radius": 1.85 * mm});
            skCircle(sketch, "E115.4.0.6", {"center": v(138.34, -53.66) * mm, "radius": 1.85 * mm});
            skCircle(sketch, "E115.4.0.7", {"center": v(136, -48) * mm, "radius": 1.85 * mm});
            skCircle(sketch, "E115.4.0.8", {"center": v(138.34, -42.34) * mm, "radius": 1.85 * mm});
            skCircle(sketch, "E115.4.1.0", {"center": v(144, -80) * mm, "radius": 4 * mm});
            skCircle(sketch, "E115.4.1.1", {"center": v(144, -72) * mm, "radius": 1.85 * mm});
            skCircle(sketch, "E115.4.1.2", {"center": v(149.66, -74.34) * mm, "radius": 1.85 * mm});
            skCircle(sketch, "E115.4.1.3", {"center": v(152, -80) * mm, "radius": 1.85 * mm});
            skCircle(sketch, "E115.4.1.4", {"center": v(149.66, -85.66) * mm, "radius": 1.85 * mm});
            skCircle(sketch, "E115.4.1.5", {"center": v(144, -88) * mm, "radius": 1.85 * mm});
            skCircle(sketch, "E115.4.1.6", {"center": v(138.34, -85.66) * mm, "radius": 1.85 * mm});
            skCircle(sketch, "E115.4.1.7", {"center": v(136, -80) * mm, "radius": 1.85 * mm});
            skCircle(sketch, "E115.4.1.8", {"center": v(138.34, -74.34) * mm, "radius": 1.85 * mm});
            skCircle(sketch, "E115.4.2.0", {"center": v(144, -112) * mm, "radius": 4 * mm});
            skCircle(sketch, "E115.4.2.1", {"center": v(144, -104) * mm, "radius": 1.85 * mm});
            skCircle(sketch, "E115.4.2.2", {"center": v(149.66, -106.34) * mm, "radius": 1.85 * mm});
            skCircle(sketch, "E115.4.2.3", {"center": v(152, -112) * mm, "radius": 1.85 * mm});
            skCircle(sketch, "E115.4.2.4", {"center": v(149.66, -117.66) * mm, "radius": 1.85 * mm});
            skCircle(sketch, "E115.4.2.5", {"center": v(144, -120) * mm, "radius": 1.85 * mm});
            skCircle(sketch, "E115.4.2.6", {"center": v(138.34, -117.66) * mm, "radius": 1.85 * mm});
            skCircle(sketch, "E115.4.2.7", {"center": v(136, -112) * mm, "radius": 1.85 * mm});
            skCircle(sketch, "E115.4.2.8", {"center": v(138.34, -106.34) * mm, "radius": 1.85 * mm});
            skCircle(sketch, "E115.4.3.0", {"center": v(144, -144) * mm, "radius": 4 * mm});
            skCircle(sketch, "E115.4.3.1", {"center": v(144, -136) * mm, "radius": 1.85 * mm});
            skCircle(sketch, "E115.4.3.2", {"center": v(149.66, -138.34) * mm, "radius": 1.85 * mm});
            skCircle(sketch, "E115.4.3.3", {"center": v(152, -144) * mm, "radius": 1.85 * mm});
            skCircle(sketch, "E115.4.3.4", {"center": v(149.66, -149.66) * mm, "radius": 1.85 * mm});
            skCircle(sketch, "E115.4.3.5", {"center": v(144, -152) * mm, "radius": 1.85 * mm});
            skCircle(sketch, "E115.4.3.6", {"center": v(138.34, -149.66) * mm, "radius": 1.85 * mm});
            skCircle(sketch, "E115.4.3.7", {"center": v(136, -144) * mm, "radius": 1.85 * mm});
            skCircle(sketch, "E115.4.3.8", {"center": v(138.34, -138.34) * mm, "radius": 1.85 * mm});
            skCircle(sketch, "E115.4.4.0", {"center": v(144, -176) * mm, "radius": 4 * mm});
            skCircle(sketch, "E115.4.4.1", {"center": v(144, -168) * mm, "radius": 1.85 * mm});
            skCircle(sketch, "E115.4.4.2", {"center": v(149.66, -170.34) * mm, "radius": 1.85 * mm});
            skCircle(sketch, "E115.4.4.3", {"center": v(152, -176) * mm, "radius": 1.85 * mm});
            skCircle(sketch, "E115.4.4.4", {"center": v(149.66, -181.66) * mm, "radius": 1.85 * mm});
            skCircle(sketch, "E115.4.4.5", {"center": v(144, -184) * mm, "radius": 1.85 * mm});
            skCircle(sketch, "E115.4.4.6", {"center": v(138.34, -181.66) * mm, "radius": 1.85 * mm});
            skCircle(sketch, "E115.4.4.7", {"center": v(136, -176) * mm, "radius": 1.85 * mm});
            skCircle(sketch, "E115.4.4.8", {"center": v(138.34, -170.34) * mm, "radius": 1.85 * mm});
            skCircle(sketch, "E115.4.5.0", {"center": v(144, -208) * mm, "radius": 4 * mm});
            skCircle(sketch, "E115.4.5.1", {"center": v(144, -200) * mm, "radius": 1.85 * mm});
            skCircle(sketch, "E115.4.5.2", {"center": v(149.66, -202.34) * mm, "radius": 1.85 * mm});
            skCircle(sketch, "E115.4.5.3", {"center": v(152, -208) * mm, "radius": 1.85 * mm});
            skCircle(sketch, "E115.4.5.4", {"center": v(149.66, -213.66) * mm, "radius": 1.85 * mm});
            skCircle(sketch, "E115.4.5.5", {"center": v(144, -216) * mm, "radius": 1.85 * mm});
            skCircle(sketch, "E115.4.5.6", {"center": v(138.34, -213.66) * mm, "radius": 1.85 * mm});
            skCircle(sketch, "E115.4.5.7", {"center": v(136, -208) * mm, "radius": 1.85 * mm});
            skCircle(sketch, "E115.4.5.8", {"center": v(138.34, -202.34) * mm, "radius": 1.85 * mm});
            skCircle(sketch, "E115.4.6.0", {"center": v(144, -240) * mm, "radius": 4 * mm});
            skCircle(sketch, "E115.4.6.1", {"center": v(144, -232) * mm, "radius": 1.85 * mm});
            skCircle(sketch, "E115.4.6.2", {"center": v(149.66, -234.34) * mm, "radius": 1.85 * mm});
            skCircle(sketch, "E115.4.6.3", {"center": v(152, -240) * mm, "radius": 1.85 * mm});
            skCircle(sketch, "E115.4.6.4", {"center": v(149.66, -245.66) * mm, "radius": 1.85 * mm});
            skCircle(sketch, "E115.4.6.5", {"center": v(144, -248) * mm, "radius": 1.85 * mm});
            skCircle(sketch, "E115.4.6.6", {"center": v(138.34, -245.66) * mm, "radius": 1.85 * mm});
            skCircle(sketch, "E115.4.6.7", {"center": v(136, -240) * mm, "radius": 1.85 * mm});
            skCircle(sketch, "E115.4.6.8", {"center": v(138.34, -234.34) * mm, "radius": 1.85 * mm});
            skCircle(sketch, "E115.5.0.0", {"center": v(176, -48) * mm, "radius": 4 * mm});
            skCircle(sketch, "E115.5.0.1", {"center": v(176, -40) * mm, "radius": 1.85 * mm});
            skCircle(sketch, "E115.5.0.2", {"center": v(181.66, -42.34) * mm, "radius": 1.85 * mm});
            skCircle(sketch, "E115.5.0.3", {"center": v(184, -48) * mm, "radius": 1.85 * mm});
            skCircle(sketch, "E115.5.0.4", {"center": v(181.66, -53.66) * mm, "radius": 1.85 * mm});
            skCircle(sketch, "E115.5.0.5", {"center": v(176, -56) * mm, "radius": 1.85 * mm});
            skCircle(sketch, "E115.5.0.6", {"center": v(170.34, -53.66) * mm, "radius": 1.85 * mm});
            skCircle(sketch, "E115.5.0.7", {"center": v(168, -48) * mm, "radius": 1.85 * mm});
            skCircle(sketch, "E115.5.0.8", {"center": v(170.34, -42.34) * mm, "radius": 1.85 * mm});
            skCircle(sketch, "E115.5.1.0", {"center": v(176, -80) * mm, "radius": 4 * mm});
            skCircle(sketch, "E115.5.1.1", {"center": v(176, -72) * mm, "radius": 1.85 * mm});
            skCircle(sketch, "E115.5.1.2", {"center": v(181.66, -74.34) * mm, "radius": 1.85 * mm});
            skCircle(sketch, "E115.5.1.3", {"center": v(184, -80) * mm, "radius": 1.85 * mm});
            skCircle(sketch, "E115.5.1.4", {"center": v(181.66, -85.66) * mm, "radius": 1.85 * mm});
            skCircle(sketch, "E115.5.1.5", {"center": v(176, -88) * mm, "radius": 1.85 * mm});
            skCircle(sketch, "E115.5.1.6", {"center": v(170.34, -85.66) * mm, "radius": 1.85 * mm});
            skCircle(sketch, "E115.5.1.7", {"center": v(168, -80) * mm, "radius": 1.85 * mm});
            skCircle(sketch, "E115.5.1.8", {"center": v(170.34, -74.34) * mm, "radius": 1.85 * mm});
            skCircle(sketch, "E115.5.2.0", {"center": v(176, -112) * mm, "radius": 4 * mm});
            skCircle(sketch, "E115.5.2.1", {"center": v(176, -104) * mm, "radius": 1.85 * mm});
            skCircle(sketch, "E115.5.2.2", {"center": v(181.66, -106.34) * mm, "radius": 1.85 * mm});
            skCircle(sketch, "E115.5.2.3", {"center": v(184, -112) * mm, "radius": 1.85 * mm});
            skCircle(sketch, "E115.5.2.4", {"center": v(181.66, -117.66) * mm, "radius": 1.85 * mm});
            skCircle(sketch, "E115.5.2.5", {"center": v(176, -120) * mm, "radius": 1.85 * mm});
            skCircle(sketch, "E115.5.2.6", {"center": v(170.34, -117.66) * mm, "radius": 1.85 * mm});
            skCircle(sketch, "E115.5.2.7", {"center": v(168, -112) * mm, "radius": 1.85 * mm});
            skCircle(sketch, "E115.5.2.8", {"center": v(170.34, -106.34) * mm, "radius": 1.85 * mm});
            skCircle(sketch, "E115.5.3.0", {"center": v(176, -144) * mm, "radius": 4 * mm});
            skCircle(sketch, "E115.5.3.1", {"center": v(176, -136) * mm, "radius": 1.85 * mm});
            skCircle(sketch, "E115.5.3.2", {"center": v(181.66, -138.34) * mm, "radius": 1.85 * mm});
            skCircle(sketch, "E115.5.3.3", {"center": v(184, -144) * mm, "radius": 1.85 * mm});
            skCircle(sketch, "E115.5.3.4", {"center": v(181.66, -149.66) * mm, "radius": 1.85 * mm});
            skCircle(sketch, "E115.5.3.5", {"center": v(176, -152) * mm, "radius": 1.85 * mm});
            skCircle(sketch, "E115.5.3.6", {"center": v(170.34, -149.66) * mm, "radius": 1.85 * mm});
            skCircle(sketch, "E115.5.3.7", {"center": v(168, -144) * mm, "radius": 1.85 * mm});
            skCircle(sketch, "E115.5.3.8", {"center": v(170.34, -138.34) * mm, "radius": 1.85 * mm});
            skCircle(sketch, "E115.5.4.0", {"center": v(176, -176) * mm, "radius": 4 * mm});
            skCircle(sketch, "E115.5.4.1", {"center": v(176, -168) * mm, "radius": 1.85 * mm});
            skCircle(sketch, "E115.5.4.2", {"center": v(181.66, -170.34) * mm, "radius": 1.85 * mm});
            skCircle(sketch, "E115.5.4.3", {"center": v(184, -176) * mm, "radius": 1.85 * mm});
            skCircle(sketch, "E115.5.4.4", {"center": v(181.66, -181.66) * mm, "radius": 1.85 * mm});
            skCircle(sketch, "E115.5.4.5", {"center": v(176, -184) * mm, "radius": 1.85 * mm});
            skCircle(sketch, "E115.5.4.6", {"center": v(170.34, -181.66) * mm, "radius": 1.85 * mm});
            skCircle(sketch, "E115.5.4.7", {"center": v(168, -176) * mm, "radius": 1.85 * mm});
            skCircle(sketch, "E115.5.4.8", {"center": v(170.34, -170.34) * mm, "radius": 1.85 * mm});
            skCircle(sketch, "E115.5.5.0", {"center": v(176, -208) * mm, "radius": 4 * mm});
            skCircle(sketch, "E115.5.5.1", {"center": v(176, -200) * mm, "radius": 1.85 * mm});
            skCircle(sketch, "E115.5.5.2", {"center": v(181.66, -202.34) * mm, "radius": 1.85 * mm});
            skCircle(sketch, "E115.5.5.3", {"center": v(184, -208) * mm, "radius": 1.85 * mm});
            skCircle(sketch, "E115.5.5.4", {"center": v(181.66, -213.66) * mm, "radius": 1.85 * mm});
            skCircle(sketch, "E115.5.5.5", {"center": v(176, -216) * mm, "radius": 1.85 * mm});
            skCircle(sketch, "E115.5.5.6", {"center": v(170.34, -213.66) * mm, "radius": 1.85 * mm});
            skCircle(sketch, "E115.5.5.7", {"center": v(168, -208) * mm, "radius": 1.85 * mm});
            skCircle(sketch, "E115.5.5.8", {"center": v(170.34, -202.34) * mm, "radius": 1.85 * mm});
            skCircle(sketch, "E115.5.6.0", {"center": v(176, -240) * mm, "radius": 4 * mm});
            skCircle(sketch, "E115.5.6.1", {"center": v(176, -232) * mm, "radius": 1.85 * mm});
            skCircle(sketch, "E115.5.6.2", {"center": v(181.66, -234.34) * mm, "radius": 1.85 * mm});
            skCircle(sketch, "E115.5.6.3", {"center": v(184, -240) * mm, "radius": 1.85 * mm});
            skCircle(sketch, "E115.5.6.4", {"center": v(181.66, -245.66) * mm, "radius": 1.85 * mm});
            skCircle(sketch, "E115.5.6.5", {"center": v(176, -248) * mm, "radius": 1.85 * mm});
            skCircle(sketch, "E115.5.6.6", {"center": v(170.34, -245.66) * mm, "radius": 1.85 * mm});
            skCircle(sketch, "E115.5.6.7", {"center": v(168, -240) * mm, "radius": 1.85 * mm});
            skCircle(sketch, "E115.5.6.8", {"center": v(170.34, -234.34) * mm, "radius": 1.85 * mm});
            skCircle(sketch, "E115.6.0.0", {"center": v(208, -48) * mm, "radius": 4 * mm});
            skCircle(sketch, "E115.6.0.1", {"center": v(208, -40) * mm, "radius": 1.85 * mm});
            skCircle(sketch, "E115.6.0.2", {"center": v(213.66, -42.34) * mm, "radius": 1.85 * mm});
            skCircle(sketch, "E115.6.0.3", {"center": v(216, -48) * mm, "radius": 1.85 * mm});
            skCircle(sketch, "E115.6.0.4", {"center": v(213.66, -53.66) * mm, "radius": 1.85 * mm});
            skCircle(sketch, "E115.6.0.5", {"center": v(208, -56) * mm, "radius": 1.85 * mm});
            skCircle(sketch, "E115.6.0.6", {"center": v(202.34, -53.66) * mm, "radius": 1.85 * mm});
            skCircle(sketch, "E115.6.0.7", {"center": v(200, -48) * mm, "radius": 1.85 * mm});
            skCircle(sketch, "E115.6.0.8", {"center": v(202.34, -42.34) * mm, "radius": 1.85 * mm});
            skCircle(sketch, "E115.6.1.0", {"center": v(208, -80) * mm, "radius": 4 * mm});
            skCircle(sketch, "E115.6.1.1", {"center": v(208, -72) * mm, "radius": 1.85 * mm});
            skCircle(sketch, "E115.6.1.2", {"center": v(213.66, -74.34) * mm, "radius": 1.85 * mm});
            skCircle(sketch, "E115.6.1.3", {"center": v(216, -80) * mm, "radius": 1.85 * mm});
            skCircle(sketch, "E115.6.1.4", {"center": v(213.66, -85.66) * mm, "radius": 1.85 * mm});
            skCircle(sketch, "E115.6.1.5", {"center": v(208, -88) * mm, "radius": 1.85 * mm});
            skCircle(sketch, "E115.6.1.6", {"center": v(202.34, -85.66) * mm, "radius": 1.85 * mm});
            skCircle(sketch, "E115.6.1.7", {"center": v(200, -80) * mm, "radius": 1.85 * mm});
            skCircle(sketch, "E115.6.1.8", {"center": v(202.34, -74.34) * mm, "radius": 1.85 * mm});
            skCircle(sketch, "E115.6.2.0", {"center": v(208, -112) * mm, "radius": 4 * mm});
            skCircle(sketch, "E115.6.2.1", {"center": v(208, -104) * mm, "radius": 1.85 * mm});
            skCircle(sketch, "E115.6.2.2", {"center": v(213.66, -106.34) * mm, "radius": 1.85 * mm});
            skCircle(sketch, "E115.6.2.3", {"center": v(216, -112) * mm, "radius": 1.85 * mm});
            skCircle(sketch, "E115.6.2.4", {"center": v(213.66, -117.66) * mm, "radius": 1.85 * mm});
            skCircle(sketch, "E115.6.2.5", {"center": v(208, -120) * mm, "radius": 1.85 * mm});
            skCircle(sketch, "E115.6.2.6", {"center": v(202.34, -117.66) * mm, "radius": 1.85 * mm});
            skCircle(sketch, "E115.6.2.7", {"center": v(200, -112) * mm, "radius": 1.85 * mm});
            skCircle(sketch, "E115.6.2.8", {"center": v(202.34, -106.34) * mm, "radius": 1.85 * mm});
            skCircle(sketch, "E115.6.3.0", {"center": v(208, -144) * mm, "radius": 4 * mm});
            skCircle(sketch, "E115.6.3.1", {"center": v(208, -136) * mm, "radius": 1.85 * mm});
            skCircle(sketch, "E115.6.3.2", {"center": v(213.66, -138.34) * mm, "radius": 1.85 * mm});
            skCircle(sketch, "E115.6.3.3", {"center": v(216, -144) * mm, "radius": 1.85 * mm});
            skCircle(sketch, "E115.6.3.4", {"center": v(213.66, -149.66) * mm, "radius": 1.85 * mm});
            skCircle(sketch, "E115.6.3.5", {"center": v(208, -152) * mm, "radius": 1.85 * mm});
            skCircle(sketch, "E115.6.3.6", {"center": v(202.34, -149.66) * mm, "radius": 1.85 * mm});
            skCircle(sketch, "E115.6.3.7", {"center": v(200, -144) * mm, "radius": 1.85 * mm});
            skCircle(sketch, "E115.6.3.8", {"center": v(202.34, -138.34) * mm, "radius": 1.85 * mm});
            skCircle(sketch, "E115.6.4.0", {"center": v(208, -176) * mm, "radius": 4 * mm});
            skCircle(sketch, "E115.6.4.1", {"center": v(208, -168) * mm, "radius": 1.85 * mm});
            skCircle(sketch, "E115.6.4.2", {"center": v(213.66, -170.34) * mm, "radius": 1.85 * mm});
            skCircle(sketch, "E115.6.4.3", {"center": v(216, -176) * mm, "radius": 1.85 * mm});
            skCircle(sketch, "E115.6.4.4", {"center": v(213.66, -181.66) * mm, "radius": 1.85 * mm});
            skCircle(sketch, "E115.6.4.5", {"center": v(208, -184) * mm, "radius": 1.85 * mm});
            skCircle(sketch, "E115.6.4.6", {"center": v(202.34, -181.66) * mm, "radius": 1.85 * mm});
            skCircle(sketch, "E115.6.4.7", {"center": v(200, -176) * mm, "radius": 1.85 * mm});
            skCircle(sketch, "E115.6.4.8", {"center": v(202.34, -170.34) * mm, "radius": 1.85 * mm});
            skCircle(sketch, "E115.6.5.0", {"center": v(208, -208) * mm, "radius": 4 * mm});
            skCircle(sketch, "E115.6.5.1", {"center": v(208, -200) * mm, "radius": 1.85 * mm});
            skCircle(sketch, "E115.6.5.2", {"center": v(213.66, -202.34) * mm, "radius": 1.85 * mm});
            skCircle(sketch, "E115.6.5.3", {"center": v(216, -208) * mm, "radius": 1.85 * mm});
            skCircle(sketch, "E115.6.5.4", {"center": v(213.66, -213.66) * mm, "radius": 1.85 * mm});
            skCircle(sketch, "E115.6.5.5", {"center": v(208, -216) * mm, "radius": 1.85 * mm});
            skCircle(sketch, "E115.6.5.6", {"center": v(202.34, -213.66) * mm, "radius": 1.85 * mm});
            skCircle(sketch, "E115.6.5.7", {"center": v(200, -208) * mm, "radius": 1.85 * mm});
            skCircle(sketch, "E115.6.5.8", {"center": v(202.34, -202.34) * mm, "radius": 1.85 * mm});
            skCircle(sketch, "E115.6.6.0", {"center": v(208, -240) * mm, "radius": 4 * mm});
            skCircle(sketch, "E115.6.6.1", {"center": v(208, -232) * mm, "radius": 1.85 * mm});
            skCircle(sketch, "E115.6.6.2", {"center": v(213.66, -234.34) * mm, "radius": 1.85 * mm});
            skCircle(sketch, "E115.6.6.3", {"center": v(216, -240) * mm, "radius": 1.85 * mm});
            skCircle(sketch, "E115.6.6.4", {"center": v(213.66, -245.66) * mm, "radius": 1.85 * mm});
            skCircle(sketch, "E115.6.6.5", {"center": v(208, -248) * mm, "radius": 1.85 * mm});
            skCircle(sketch, "E115.6.6.6", {"center": v(202.34, -245.66) * mm, "radius": 1.85 * mm});
            skCircle(sketch, "E115.6.6.7", {"center": v(200, -240) * mm, "radius": 1.85 * mm});
            skCircle(sketch, "E115.6.6.8", {"center": v(202.34, -234.34) * mm, "radius": 1.85 * mm});
            skLineSegment(sketch, "E115.direction1", {"start": v(16, -48) * mm, "end": v(48, -48) * mm, "construction": true});
            skLineSegment(sketch, "E115.direction2", {"start": v(16, -48) * mm, "end": v(16, -80) * mm, "construction": true});
            skCircle(sketch, "E116.0.7.0", {"center": v(240, -48) * mm, "radius": 4 * mm});
            skCircle(sketch, "E116.2.7.0", {"center": v(240, -40) * mm, "radius": 1.85 * mm});
            skCircle(sketch, "E116.4.7.0", {"center": v(245.66, -42.34) * mm, "radius": 1.85 * mm});
            skCircle(sketch, "E116.6.7.0", {"center": v(248, -48) * mm, "radius": 1.85 * mm});
            skCircle(sketch, "E116.8.7.0", {"center": v(245.66, -53.66) * mm, "radius": 1.85 * mm});
            skCircle(sketch, "E116.10.7.0", {"center": v(240, -56) * mm, "radius": 1.85 * mm});
            skCircle(sketch, "E116.12.7.0", {"center": v(234.34, -53.66) * mm, "radius": 1.85 * mm});
            skCircle(sketch, "E116.14.7.0", {"center": v(232, -48) * mm, "radius": 1.85 * mm});
            skCircle(sketch, "E116.16.7.0", {"center": v(234.34, -42.34) * mm, "radius": 1.85 * mm});
            skCircle(sketch, "E116.0.7.1", {"center": v(240, -80) * mm, "radius": 4 * mm});
            skCircle(sketch, "E116.2.7.1", {"center": v(240, -72) * mm, "radius": 1.85 * mm});
            skCircle(sketch, "E116.4.7.1", {"center": v(245.66, -74.34) * mm, "radius": 1.85 * mm});
            skCircle(sketch, "E116.6.7.1", {"center": v(248, -80) * mm, "radius": 1.85 * mm});
            skCircle(sketch, "E116.8.7.1", {"center": v(245.66, -85.66) * mm, "radius": 1.85 * mm});
            skCircle(sketch, "E116.10.7.1", {"center": v(240, -88) * mm, "radius": 1.85 * mm});
            skCircle(sketch, "E116.12.7.1", {"center": v(234.34, -85.66) * mm, "radius": 1.85 * mm});
            skCircle(sketch, "E116.14.7.1", {"center": v(232, -80) * mm, "radius": 1.85 * mm});
            skCircle(sketch, "E116.16.7.1", {"center": v(234.34, -74.34) * mm, "radius": 1.85 * mm});
            skCircle(sketch, "E116.0.7.2", {"center": v(240, -112) * mm, "radius": 4 * mm});
            skCircle(sketch, "E116.2.7.2", {"center": v(240, -104) * mm, "radius": 1.85 * mm});
            skCircle(sketch, "E116.4.7.2", {"center": v(245.66, -106.34) * mm, "radius": 1.85 * mm});
            skCircle(sketch, "E116.6.7.2", {"center": v(248, -112) * mm, "radius": 1.85 * mm});
            skCircle(sketch, "E116.8.7.2", {"center": v(245.66, -117.66) * mm, "radius": 1.85 * mm});
            skCircle(sketch, "E116.10.7.2", {"center": v(240, -120) * mm, "radius": 1.85 * mm});
            skCircle(sketch, "E116.12.7.2", {"center": v(234.34, -117.66) * mm, "radius": 1.85 * mm});
            skCircle(sketch, "E116.14.7.2", {"center": v(232, -112) * mm, "radius": 1.85 * mm});
            skCircle(sketch, "E116.16.7.2", {"center": v(234.34, -106.34) * mm, "radius": 1.85 * mm});
            skCircle(sketch, "E116.0.7.3", {"center": v(240, -144) * mm, "radius": 4 * mm});
            skCircle(sketch, "E116.2.7.3", {"center": v(240, -136) * mm, "radius": 1.85 * mm});
            skCircle(sketch, "E116.4.7.3", {"center": v(245.66, -138.34) * mm, "radius": 1.85 * mm});
            skCircle(sketch, "E116.6.7.3", {"center": v(248, -144) * mm, "radius": 1.85 * mm});
            skCircle(sketch, "E116.8.7.3", {"center": v(245.66, -149.66) * mm, "radius": 1.85 * mm});
            skCircle(sketch, "E116.10.7.3", {"center": v(240, -152) * mm, "radius": 1.85 * mm});
            skCircle(sketch, "E116.12.7.3", {"center": v(234.34, -149.66) * mm, "radius": 1.85 * mm});
            skCircle(sketch, "E116.14.7.3", {"center": v(232, -144) * mm, "radius": 1.85 * mm});
            skCircle(sketch, "E116.16.7.3", {"center": v(234.34, -138.34) * mm, "radius": 1.85 * mm});
            skCircle(sketch, "E116.0.7.4", {"center": v(240, -176) * mm, "radius": 4 * mm});
            skCircle(sketch, "E116.2.7.4", {"center": v(240, -168) * mm, "radius": 1.85 * mm});
            skCircle(sketch, "E116.4.7.4", {"center": v(245.66, -170.34) * mm, "radius": 1.85 * mm});
            skCircle(sketch, "E116.6.7.4", {"center": v(248, -176) * mm, "radius": 1.85 * mm});
            skCircle(sketch, "E116.8.7.4", {"center": v(245.66, -181.66) * mm, "radius": 1.85 * mm});
            skCircle(sketch, "E116.10.7.4", {"center": v(240, -184) * mm, "radius": 1.85 * mm});
            skCircle(sketch, "E116.12.7.4", {"center": v(234.34, -181.66) * mm, "radius": 1.85 * mm});
            skCircle(sketch, "E116.14.7.4", {"center": v(232, -176) * mm, "radius": 1.85 * mm});
            skCircle(sketch, "E116.16.7.4", {"center": v(234.34, -170.34) * mm, "radius": 1.85 * mm});
            skCircle(sketch, "E116.0.7.5", {"center": v(240, -208) * mm, "radius": 4 * mm});
            skCircle(sketch, "E116.2.7.5", {"center": v(240, -200) * mm, "radius": 1.85 * mm});
            skCircle(sketch, "E116.4.7.5", {"center": v(245.66, -202.34) * mm, "radius": 1.85 * mm});
            skCircle(sketch, "E116.6.7.5", {"center": v(248, -208) * mm, "radius": 1.85 * mm});
            skCircle(sketch, "E116.8.7.5", {"center": v(245.66, -213.66) * mm, "radius": 1.85 * mm});
            skCircle(sketch, "E116.10.7.5", {"center": v(240, -216) * mm, "radius": 1.85 * mm});
            skCircle(sketch, "E116.12.7.5", {"center": v(234.34, -213.66) * mm, "radius": 1.85 * mm});
            skCircle(sketch, "E116.14.7.5", {"center": v(232, -208) * mm, "radius": 1.85 * mm});
            skCircle(sketch, "E116.16.7.5", {"center": v(234.34, -202.34) * mm, "radius": 1.85 * mm});
            skCircle(sketch, "E116.0.7.6", {"center": v(240, -240) * mm, "radius": 4 * mm});
            skCircle(sketch, "E116.2.7.6", {"center": v(240, -232) * mm, "radius": 1.85 * mm});
            skCircle(sketch, "E116.4.7.6", {"center": v(245.66, -234.34) * mm, "radius": 1.85 * mm});
            skCircle(sketch, "E116.6.7.6", {"center": v(248, -240) * mm, "radius": 1.85 * mm});
            skCircle(sketch, "E116.8.7.6", {"center": v(245.66, -245.66) * mm, "radius": 1.85 * mm});
            skCircle(sketch, "E116.10.7.6", {"center": v(240, -248) * mm, "radius": 1.85 * mm});
            skCircle(sketch, "E116.12.7.6", {"center": v(234.34, -245.66) * mm, "radius": 1.85 * mm});
            skCircle(sketch, "E116.14.7.6", {"center": v(232, -240) * mm, "radius": 1.85 * mm});
            skCircle(sketch, "E116.16.7.6", {"center": v(234.34, -234.34) * mm, "radius": 1.85 * mm});
            skCircle(sketch, "E116.0.8.0", {"center": v(272, -48) * mm, "radius": 4 * mm});
            skCircle(sketch, "E116.2.8.0", {"center": v(272, -40) * mm, "radius": 1.85 * mm});
            skCircle(sketch, "E116.4.8.0", {"center": v(277.66, -42.34) * mm, "radius": 1.85 * mm});
            skCircle(sketch, "E116.6.8.0", {"center": v(280, -48) * mm, "radius": 1.85 * mm});
            skCircle(sketch, "E116.8.8.0", {"center": v(277.66, -53.66) * mm, "radius": 1.85 * mm});
            skCircle(sketch, "E116.10.8.0", {"center": v(272, -56) * mm, "radius": 1.85 * mm});
            skCircle(sketch, "E116.12.8.0", {"center": v(266.34, -53.66) * mm, "radius": 1.85 * mm});
            skCircle(sketch, "E116.14.8.0", {"center": v(264, -48) * mm, "radius": 1.85 * mm});
            skCircle(sketch, "E116.16.8.0", {"center": v(266.34, -42.34) * mm, "radius": 1.85 * mm});
            skCircle(sketch, "E116.0.8.1", {"center": v(272, -80) * mm, "radius": 4 * mm});
            skCircle(sketch, "E116.2.8.1", {"center": v(272, -72) * mm, "radius": 1.85 * mm});
            skCircle(sketch, "E116.4.8.1", {"center": v(277.66, -74.34) * mm, "radius": 1.85 * mm});
            skCircle(sketch, "E116.6.8.1", {"center": v(280, -80) * mm, "radius": 1.85 * mm});
            skCircle(sketch, "E116.8.8.1", {"center": v(277.66, -85.66) * mm, "radius": 1.85 * mm});
            skCircle(sketch, "E116.10.8.1", {"center": v(272, -88) * mm, "radius": 1.85 * mm});
            skCircle(sketch, "E116.12.8.1", {"center": v(266.34, -85.66) * mm, "radius": 1.85 * mm});
            skCircle(sketch, "E116.14.8.1", {"center": v(264, -80) * mm, "radius": 1.85 * mm});
            skCircle(sketch, "E116.16.8.1", {"center": v(266.34, -74.34) * mm, "radius": 1.85 * mm});
            skCircle(sketch, "E116.0.8.2", {"center": v(272, -112) * mm, "radius": 4 * mm});
            skCircle(sketch, "E116.2.8.2", {"center": v(272, -104) * mm, "radius": 1.85 * mm});
            skCircle(sketch, "E116.4.8.2", {"center": v(277.66, -106.34) * mm, "radius": 1.85 * mm});
            skCircle(sketch, "E116.6.8.2", {"center": v(280, -112) * mm, "radius": 1.85 * mm});
            skCircle(sketch, "E116.8.8.2", {"center": v(277.66, -117.66) * mm, "radius": 1.85 * mm});
            skCircle(sketch, "E116.10.8.2", {"center": v(272, -120) * mm, "radius": 1.85 * mm});
            skCircle(sketch, "E116.12.8.2", {"center": v(266.34, -117.66) * mm, "radius": 1.85 * mm});
            skCircle(sketch, "E116.14.8.2", {"center": v(264, -112) * mm, "radius": 1.85 * mm});
            skCircle(sketch, "E116.16.8.2", {"center": v(266.34, -106.34) * mm, "radius": 1.85 * mm});
            skCircle(sketch, "E116.0.8.3", {"center": v(272, -144) * mm, "radius": 4 * mm});
            skCircle(sketch, "E116.2.8.3", {"center": v(272, -136) * mm, "radius": 1.85 * mm});
            skCircle(sketch, "E116.4.8.3", {"center": v(277.66, -138.34) * mm, "radius": 1.85 * mm});
            skCircle(sketch, "E116.6.8.3", {"center": v(280, -144) * mm, "radius": 1.85 * mm});
            skCircle(sketch, "E116.8.8.3", {"center": v(277.66, -149.66) * mm, "radius": 1.85 * mm});
            skCircle(sketch, "E116.10.8.3", {"center": v(272, -152) * mm, "radius": 1.85 * mm});
            skCircle(sketch, "E116.12.8.3", {"center": v(266.34, -149.66) * mm, "radius": 1.85 * mm});
            skCircle(sketch, "E116.14.8.3", {"center": v(264, -144) * mm, "radius": 1.85 * mm});
            skCircle(sketch, "E116.16.8.3", {"center": v(266.34, -138.34) * mm, "radius": 1.85 * mm});
            skCircle(sketch, "E116.0.8.4", {"center": v(272, -176) * mm, "radius": 4 * mm});
            skCircle(sketch, "E116.2.8.4", {"center": v(272, -168) * mm, "radius": 1.85 * mm});
            skCircle(sketch, "E116.4.8.4", {"center": v(277.66, -170.34) * mm, "radius": 1.85 * mm});
            skCircle(sketch, "E116.6.8.4", {"center": v(280, -176) * mm, "radius": 1.85 * mm});
            skCircle(sketch, "E116.8.8.4", {"center": v(277.66, -181.66) * mm, "radius": 1.85 * mm});
            skCircle(sketch, "E116.10.8.4", {"center": v(272, -184) * mm, "radius": 1.85 * mm});
            skCircle(sketch, "E116.12.8.4", {"center": v(266.34, -181.66) * mm, "radius": 1.85 * mm});
            skCircle(sketch, "E116.14.8.4", {"center": v(264, -176) * mm, "radius": 1.85 * mm});
            skCircle(sketch, "E116.16.8.4", {"center": v(266.34, -170.34) * mm, "radius": 1.85 * mm});
            skCircle(sketch, "E116.0.8.5", {"center": v(272, -208) * mm, "radius": 4 * mm});
            skCircle(sketch, "E116.2.8.5", {"center": v(272, -200) * mm, "radius": 1.85 * mm});
            skCircle(sketch, "E116.4.8.5", {"center": v(277.66, -202.34) * mm, "radius": 1.85 * mm});
            skCircle(sketch, "E116.6.8.5", {"center": v(280, -208) * mm, "radius": 1.85 * mm});
            skCircle(sketch, "E116.8.8.5", {"center": v(277.66, -213.66) * mm, "radius": 1.85 * mm});
            skCircle(sketch, "E116.10.8.5", {"center": v(272, -216) * mm, "radius": 1.85 * mm});
            skCircle(sketch, "E116.12.8.5", {"center": v(266.34, -213.66) * mm, "radius": 1.85 * mm});
            skCircle(sketch, "E116.14.8.5", {"center": v(264, -208) * mm, "radius": 1.85 * mm});
            skCircle(sketch, "E116.16.8.5", {"center": v(266.34, -202.34) * mm, "radius": 1.85 * mm});
            skCircle(sketch, "E116.0.8.6", {"center": v(272, -240) * mm, "radius": 4 * mm});
            skCircle(sketch, "E116.2.8.6", {"center": v(272, -232) * mm, "radius": 1.85 * mm});
            skCircle(sketch, "E116.4.8.6", {"center": v(277.66, -234.34) * mm, "radius": 1.85 * mm});
            skCircle(sketch, "E116.6.8.6", {"center": v(280, -240) * mm, "radius": 1.85 * mm});
            skCircle(sketch, "E116.8.8.6", {"center": v(277.66, -245.66) * mm, "radius": 1.85 * mm});
            skCircle(sketch, "E116.10.8.6", {"center": v(272, -248) * mm, "radius": 1.85 * mm});
            skCircle(sketch, "E116.12.8.6", {"center": v(266.34, -245.66) * mm, "radius": 1.85 * mm});
            skCircle(sketch, "E116.14.8.6", {"center": v(264, -240) * mm, "radius": 1.85 * mm});
            skCircle(sketch, "E116.16.8.6", {"center": v(266.34, -234.34) * mm, "radius": 1.85 * mm});
            skCircle(sketch, "E117", {"center": v(171, -362.66) * mm, "radius": 1.3 * mm});
            skCircle(sketch, "E118.0.1.0", {"center": v(155.8, -311.86) * mm, "radius": 1.3 * mm});
            skCircle(sketch, "E118.1.0.0", {"center": v(198.9, -362.66) * mm, "radius": 1.3 * mm});
            skCircle(sketch, "E118.1.1.0", {"center": v(204, -310.56) * mm, "radius": 1.3 * mm});
            skSolve(sketch);
        }
        {
            var Q0;
            Q0=makeQuery(id+"F0.imprint","IMPRINT",FACE,{"disambiguationData":[TD([[makeQuery(id+"F0.imprint","IMPRINT",EDGE,{"derivedFrom":sQuery(id+"F0.wireOp",EDGE,"E0.bottom")}),-1.0]])]});
            extrude(context, id + "F2", {"entities" : qUnion([Q0]), "depth" : 25 * mm, "offsetDistance" : 25 * mm});
        }
        {
            var Q0;
            Q0 = qSketchRegion(id + "F1", true);
            extrude(context, id + "F3", {"entities" : qUnion([Q0]), "operationType" : NewBodyOperationType.REMOVE, "endBound" : BoundingType.THROUGH_ALL, "depth" : 25 * mm, "offsetDistance" : 25 * mm});
        }
    });
